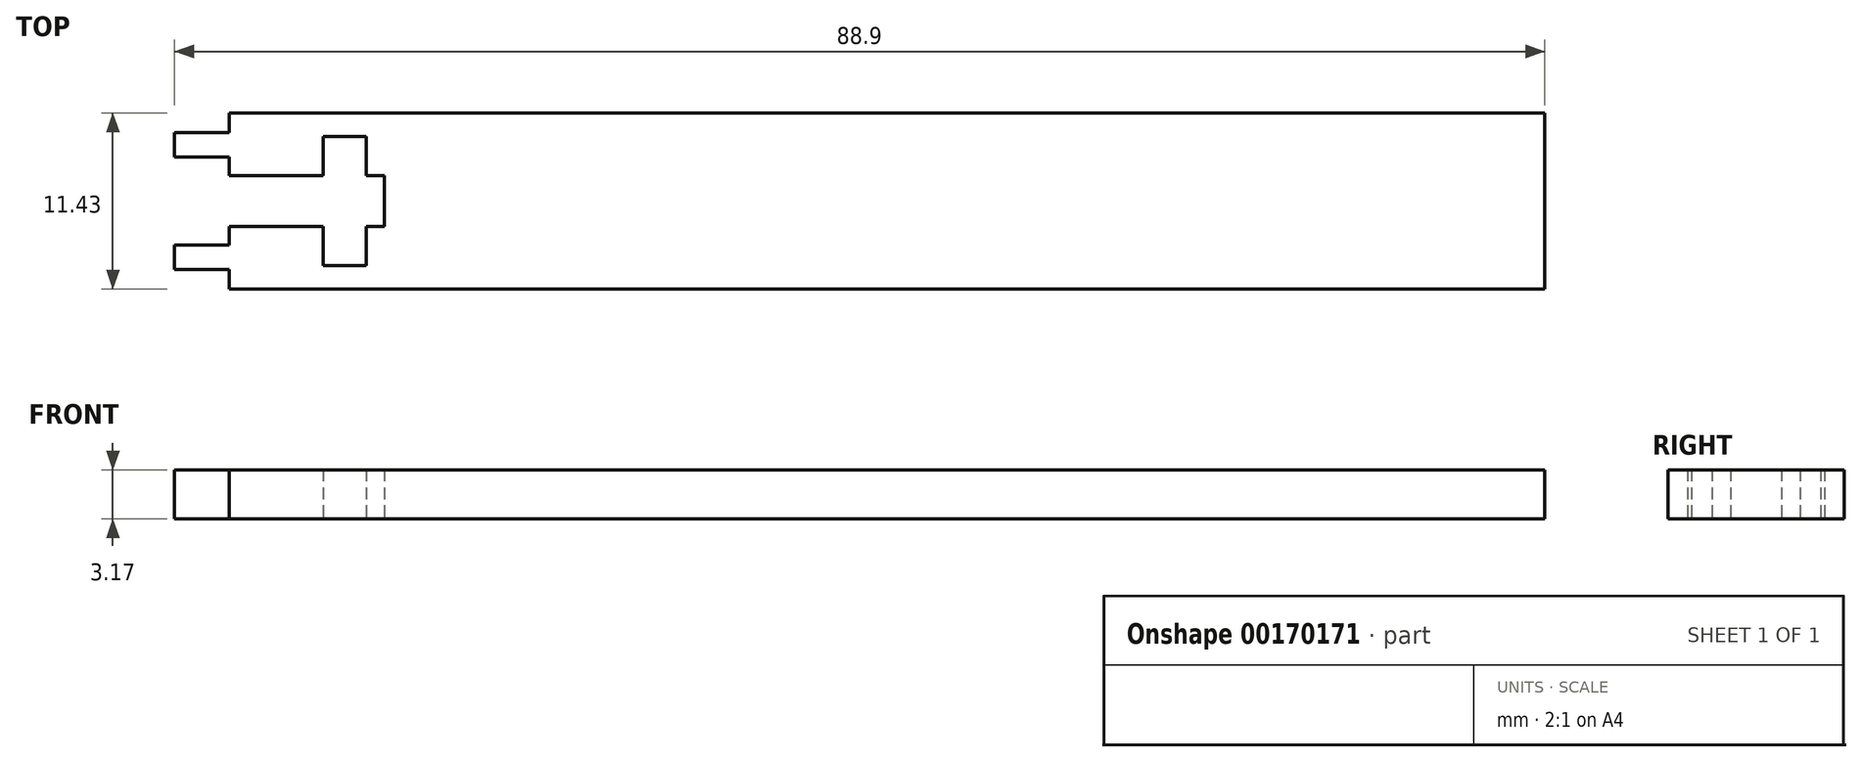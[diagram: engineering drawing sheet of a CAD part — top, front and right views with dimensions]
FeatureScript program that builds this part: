
annotation { "Feature Type Name" : "Feature", "Feature Type Description" : "" }
export const myFeature = defineFeature(function(context is Context, id is Id, definition is map)
    precondition{}
    {
        {
            var Q0;
            Q0=qCreatedBy(makeId("Top.planeOp"),FACE);
            var sketch = newSketch(context, id + "F0", { "sketchPlane" : qUnion([Q0])});
            skLineSegment(sketch, "E0.bottom", {"start": v(-41.9, 23.92) * mm, "end": v(43.44, 23.92) * mm});
            skLineSegment(sketch, "E0.top", {"start": v(-41.9, 12.5) * mm, "end": v(43.44, 12.5) * mm});
            skLineSegment(sketch, "E0.left", {"start": v(-45.46, 22.65) * mm, "end": v(-45.46, 21.06) * mm});
            skLineSegment(sketch, "E0.right", {"start": v(43.44, 23.92) * mm, "end": v(43.44, 12.5) * mm});
            skLineSegment(sketch, "E1", {"start": v(-41.9, 23.92) * mm, "end": v(-41.9, 22.65) * mm});
            skLineSegment(sketch, "E2", {"start": v(-41.9, 22.65) * mm, "end": v(-45.46, 22.65) * mm});
            skLineSegment(sketch, "E3", {"start": v(-41.9, 18.2) * mm, "end": v(-40.6, 18.2) * mm});
            skLineSegment(sketch, "E4", {"start": v(-41.9, 22.65) * mm, "end": v(-41.9, 19.86) * mm});
            skLineSegment(sketch, "E5", {"start": v(-45.46, 21.06) * mm, "end": v(-41.9, 21.06) * mm});
            skLineSegment(sketch, "E6", {"start": v(-41.9, 19.86) * mm, "end": v(-35.81, 19.86) * mm});
            skLineSegment(sketch, "E7", {"start": v(-35.81, 19.86) * mm, "end": v(-35.81, 22.4) * mm});
            skLineSegment(sketch, "E8", {"start": v(-35.81, 22.4) * mm, "end": v(-33.02, 22.4) * mm});
            skLineSegment(sketch, "E9", {"start": v(-33.02, 22.4) * mm, "end": v(-33.02, 19.86) * mm});
            skLineSegment(sketch, "E10", {"start": v(-40.6, 18.2) * mm, "end": v(-31.84, 18.2) * mm});
            skLineSegment(sketch, "E11", {"start": v(-31.84, 19.86) * mm, "end": v(-31.84, 18.2) * mm});
            skPoint(sketch, "E12.orphan", {"position": v(-45.46, 23.92) * mm});
            skLineSegment(sketch, "E13.MirrorCS", {"start": v(-35.81, 16.56) * mm, "end": v(-35.81, 14.02) * mm});
            skLineSegment(sketch, "E14.MirrorCS", {"start": v(-35.81, 14.02) * mm, "end": v(-33.02, 14.02) * mm});
            skLineSegment(sketch, "E15.MirrorCS", {"start": v(-33.02, 14.02) * mm, "end": v(-33.02, 16.56) * mm});
            skLineSegment(sketch, "E16.MirrorCS", {"start": v(-41.9, 16.56) * mm, "end": v(-35.81, 16.56) * mm});
            skLineSegment(sketch, "E17.MirrorCS", {"start": v(-31.84, 16.56) * mm, "end": v(-31.84, 18.2) * mm});
            skLineSegment(sketch, "E18.MirrorCS", {"start": v(-41.9, 13.76) * mm, "end": v(-45.46, 13.76) * mm});
            skLineSegment(sketch, "E19.MirrorCS", {"start": v(-45.46, 15.35) * mm, "end": v(-41.9, 15.35) * mm});
            skLineSegment(sketch, "E20.MirrorCS", {"start": v(-41.9, 13.76) * mm, "end": v(-41.9, 16.56) * mm});
            skPoint(sketch, "E21.orphan", {"position": v(-44.54, 19.86) * mm});
            skPoint(sketch, "E22.MirrorCS.end.orphan", {"position": v(-41.9, 16.56) * mm});
            skPoint(sketch, "E22.MirrorCS.start.orphan", {"position": v(-44.54, 16.56) * mm});
            skPoint(sketch, "E23.orphan", {"position": v(-45.46, 18.2) * mm});
            skLineSegment(sketch, "E24", {"start": v(-41.9, 13.76) * mm, "end": v(-41.9, 12.5) * mm});
            skPoint(sketch, "E25.orphan", {"position": v(-45.46, 12.5) * mm});
            skLineSegment(sketch, "E26", {"start": v(-45.46, 13.76) * mm, "end": v(-45.46, 15.35) * mm});
            skPoint(sketch, "E27.orphan", {"position": v(-41.9, 18.2) * mm});
            skLineSegment(sketch, "E28.trimOffspring", {"start": v(-33.02, 19.86) * mm, "end": v(-31.84, 19.86) * mm});
            skLineSegment(sketch, "E29.trimOffspring", {"start": v(-33.02, 16.56) * mm, "end": v(-31.84, 16.56) * mm});
            skSolve(sketch);
        }
        {
            var Q0;
            Q0=makeQuery(id+"F0.imprint","IMPRINT",FACE,{"disambiguationData":[TD([[makeQuery(id+"F0.imprint","IMPRINT",EDGE,{"derivedFrom":sQuery(id+"F0.wireOp",EDGE,"E0.left")}),1.0]])]});
            var Q1;
            {var subQ0=sQuery(id+"F0.wireOp",EDGE,"E18.MirrorCS");Q1=makeQuery(id+"F0.imprint","IMPRINT",FACE,{"disambiguationData":[TD([[makeQuery(id+"F0.imprint","IMPRINT",EDGE,{"derivedFrom":subQ0}),-1.0]])]});}
            var Q2;
            Q2=makeQuery(id+"F0.imprint","IMPRINT",FACE,{"disambiguationData":[TD([[makeQuery(id+"F0.imprint","IMPRINT",EDGE,{"derivedFrom":sQuery(id+"F0.wireOp",EDGE,"E0.bottom")}),-1.0]])]});
            extrude(context, id + "F1", {"entities" : qUnion([Q0, Q1, Q2]), "depth" : 3.17 * mm});
        }
    });
